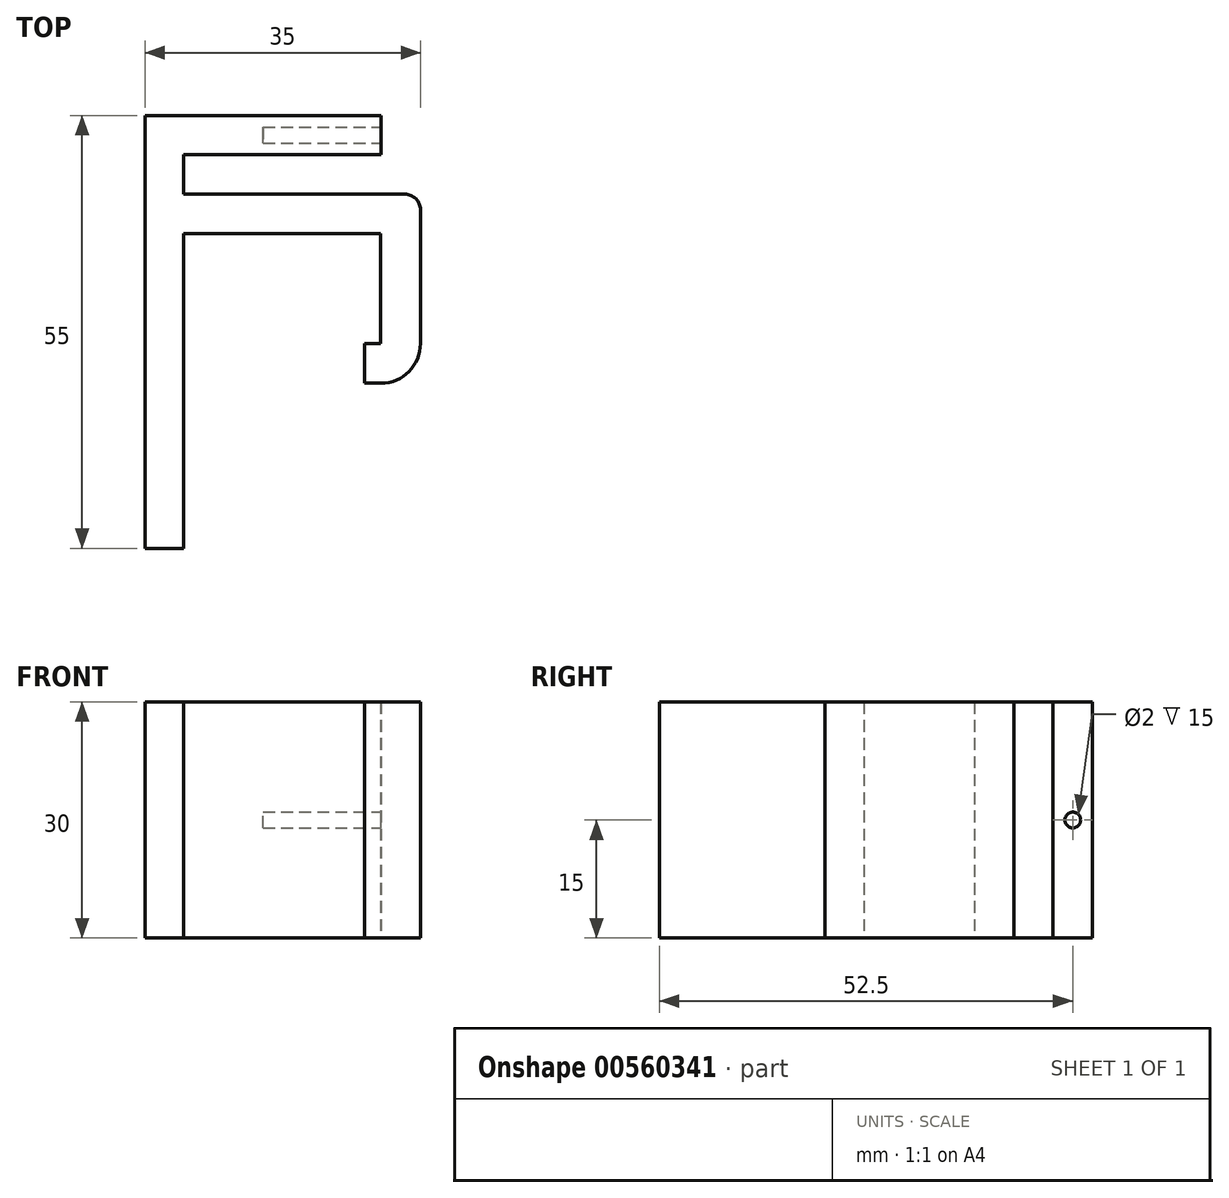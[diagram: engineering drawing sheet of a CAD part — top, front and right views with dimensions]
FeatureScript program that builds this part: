
annotation { "Feature Type Name" : "Feature", "Feature Type Description" : "" }
export const myFeature = defineFeature(function(context is Context, id is Id, definition is map)
    precondition{}
    {
        {
            var Q0;
            Q0=qCreatedBy(makeId("Top.planeOp"),FACE);
            var sketch = newSketch(context, id + "F0", { "sketchPlane" : qUnion([Q0])});
            skLineSegment(sketch, "E0", {"start": v(0, 0) * mm, "end": v(0, 45) * mm});
            skLineSegment(sketch, "E1", {"start": v(35, 43) * mm, "end": v(35, 26) * mm});
            skLineSegment(sketch, "E2", {"start": v(30, 21) * mm, "end": v(27.9, 21) * mm});
            skLineSegment(sketch, "E3", {"start": v(27.9, 21) * mm, "end": v(27.9, 26) * mm});
            skLineSegment(sketch, "E4", {"start": v(27.9, 26) * mm, "end": v(29.9, 26) * mm});
            skLineSegment(sketch, "E5", {"start": v(29.9, 26) * mm, "end": v(29.9, 40) * mm});
            skLineSegment(sketch, "E6", {"start": v(29.9, 40) * mm, "end": v(4.9, 40) * mm});
            skLineSegment(sketch, "E7", {"start": v(4.9, 40) * mm, "end": v(4.9, 0) * mm});
            skLineSegment(sketch, "E8", {"start": v(4.9, 0) * mm, "end": v(0, 0) * mm});
            skPoint(sketch, "E9.visualSharp", {"position": v(0, 45) * mm});
            skLineSegment(sketch, "E9.filletArc", {"start": v(0, 45) * mm, "end": v(0, 45) * mm});
            skPoint(sketch, "E10.visualSharp", {"position": v(35, 45) * mm});
            skArc(sketch, "E10.filletArc", {"start": v(35, 43) * mm, "mid": v(34.41, 44.41) * mm, "end": v(33, 45) * mm});
            skPoint(sketch, "E11.visualSharp", {"position": v(35, 21) * mm});
            skArc(sketch, "E11.filletArc", {"start": v(30, 21) * mm, "mid": v(33.54, 22.46) * mm, "end": v(35, 26) * mm});
            skLineSegment(sketch, "E12", {"start": v(0, 45) * mm, "end": v(0, 55) * mm});
            skLineSegment(sketch, "E13", {"start": v(0, 55) * mm, "end": v(30, 55) * mm});
            skLineSegment(sketch, "E14", {"start": v(4.9, 50) * mm, "end": v(4.9, 45) * mm});
            skLineSegment(sketch, "E15", {"start": v(30, 50) * mm, "end": v(30, 55) * mm});
            skLineSegment(sketch, "E16", {"start": v(30, 50) * mm, "end": v(4.9, 50) * mm});
            skLineSegment(sketch, "E17", {"start": v(4.9, 45) * mm, "end": v(33, 45) * mm});
            skSolve(sketch);
        }
        {
            var Q0;
            Q0=makeQuery(id+"F0.imprint","IMPRINT",FACE,{"disambiguationData":[TD([[makeQuery(id+"F0.imprint","IMPRINT",EDGE,{"derivedFrom":sQuery(id+"F0.wireOp",EDGE,"E0")}),-1.0]])]});
            extrude(context, id + "F1", {"entities" : qUnion([Q0]), "depth" : 30 * mm});
        }
        {
            var Q0;
            Q0=makeQuery(id+"F1.opExtrude","SWEPT_FACE",FACE,{"disambiguationData":[OSD([sQuery(id+"F0.wireOp",EDGE,"E15")])]});
            var sketch = newSketch(context, id + "F2", { "sketchPlane" : qUnion([Q0])});
            skCircle(sketch, "E18", {"center": v(52.5, 15) * mm, "radius": 1 * mm});
            skSolve(sketch);
        }
        {
            var Q0;
            Q0=makeQuery(id+"F2.imprint","IMPRINT",FACE,{"disambiguationData":[TD([[makeQuery(id+"F2.imprint","IMPRINT",EDGE,{"derivedFrom":sQuery(id+"F2.wireOp",EDGE,"E18")}),1.0]])]});
            extrude(context, id + "F3", {"entities" : qUnion([Q0]), "operationType" : NewBodyOperationType.REMOVE, "oppositeDirection" : true, "depth" : 15 * mm});
        }
    });
